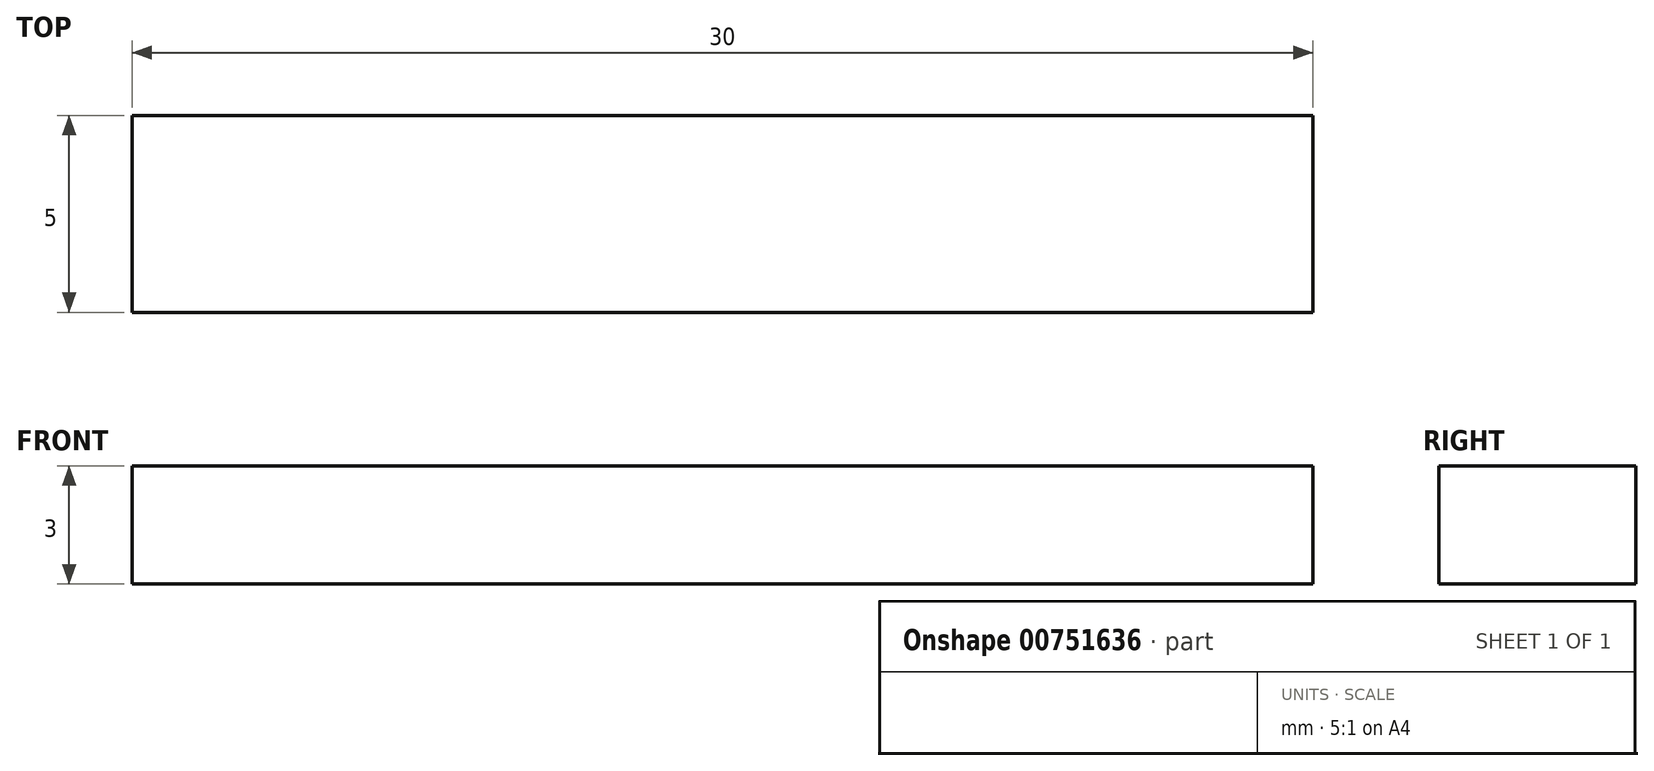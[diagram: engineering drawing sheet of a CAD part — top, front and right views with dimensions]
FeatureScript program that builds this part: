
annotation { "Feature Type Name" : "Feature", "Feature Type Description" : "" }
export const myFeature = defineFeature(function(context is Context, id is Id, definition is map)
    precondition{}
    {
        {
            var Q0;
            Q0=qCreatedBy(makeId("Top.planeOp"),FACE);
            var sketch = newSketch(context, id + "F0", { "sketchPlane" : qUnion([Q0])});
            skLineSegment(sketch, "E0.bottom", {"start": v(-15, 2.5) * mm, "end": v(15, 2.5) * mm});
            skLineSegment(sketch, "E0.top", {"start": v(-15, -2.5) * mm, "end": v(15, -2.5) * mm});
            skLineSegment(sketch, "E0.left", {"start": v(-15, 2.5) * mm, "end": v(-15, -2.5) * mm});
            skLineSegment(sketch, "E0.right", {"start": v(15, 2.5) * mm, "end": v(15, -2.5) * mm});
            skPoint(sketch, "E0.middle", {"position": v(0, 0) * mm});
            skSolve(sketch);
        }
        {
            var Q0;
            Q0 = qSketchRegion(id + "F0", true);
            extrude(context, id + "F1", {"entities" : qUnion([Q0]), "depth" : 3 * mm, "offsetDistance" : 25 * mm});
        }
    });
